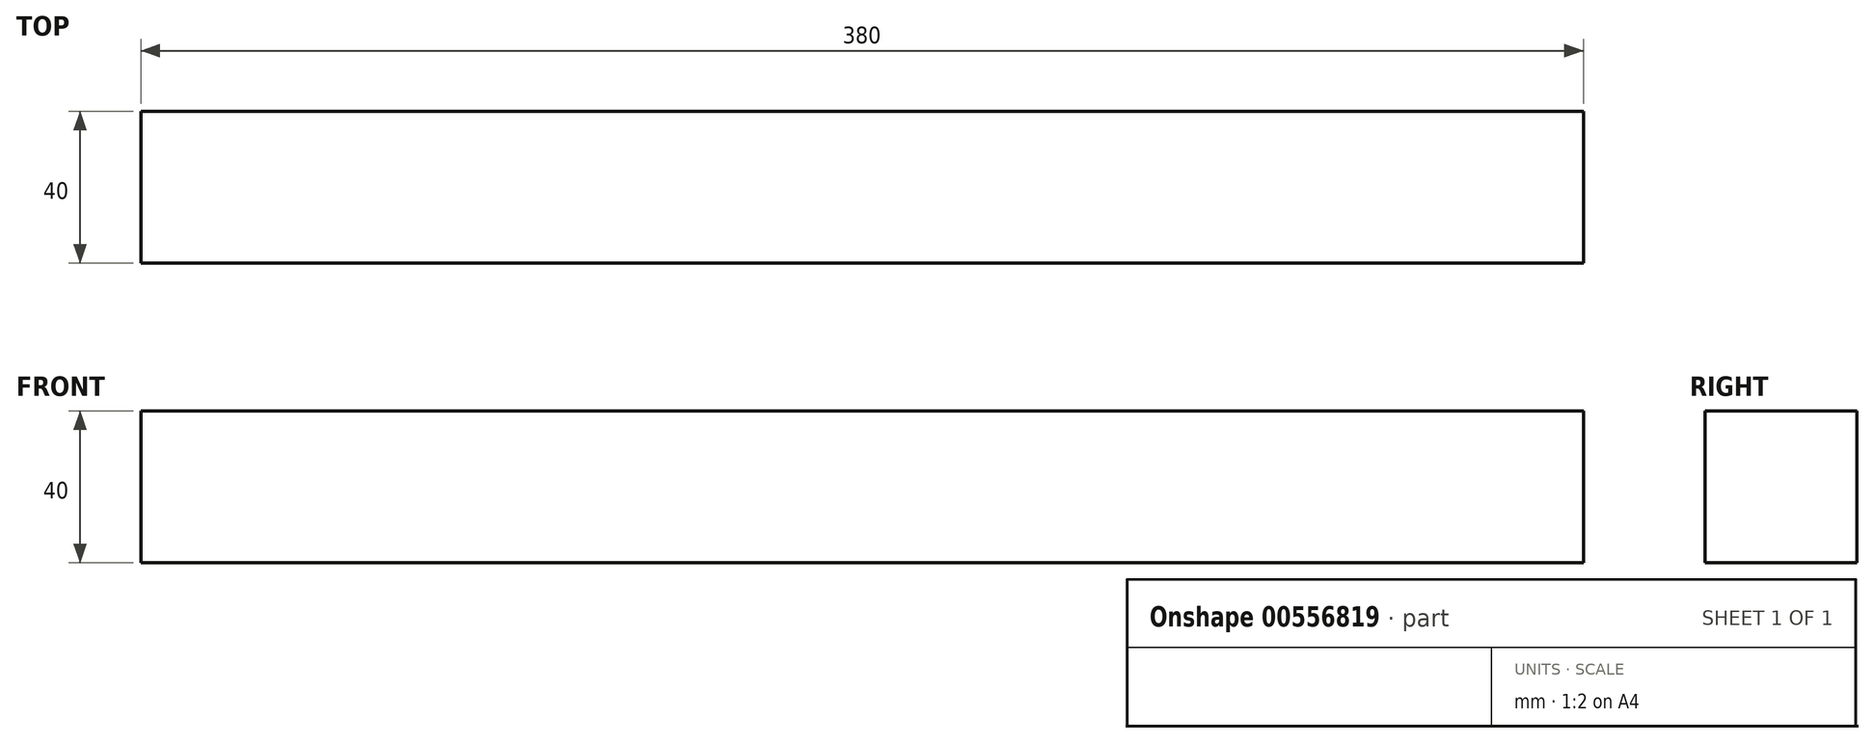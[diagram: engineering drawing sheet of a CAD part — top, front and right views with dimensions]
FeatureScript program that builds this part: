
annotation { "Feature Type Name" : "Feature", "Feature Type Description" : "" }
export const myFeature = defineFeature(function(context is Context, id is Id, definition is map)
    precondition{}
    {
        {
            var Q0;
            Q0=qCreatedBy(makeId("Front.planeOp"),FACE);
            var sketch = newSketch(context, id + "F0", { "sketchPlane" : qUnion([Q0])});
            skLineSegment(sketch, "E0.bottom", {"start": v(-190, 20) * mm, "end": v(190, 20) * mm});
            skLineSegment(sketch, "E0.top", {"start": v(-190, -20) * mm, "end": v(190, -20) * mm});
            skLineSegment(sketch, "E0.left", {"start": v(-190, 20) * mm, "end": v(-190, -20) * mm});
            skLineSegment(sketch, "E0.right", {"start": v(190, 20) * mm, "end": v(190, -20) * mm});
            skPoint(sketch, "E0.middle", {"position": v(0, 0) * mm});
            skSolve(sketch);
        }
        {
            var Q0;
            Q0=qSketchRegion(id+"F0",true);
            extrude(context, id + "F1", {"entities" : qUnion([Q0]), "depth" : 40 * mm, "offsetDistance" : 25 * mm});
        }
    });
